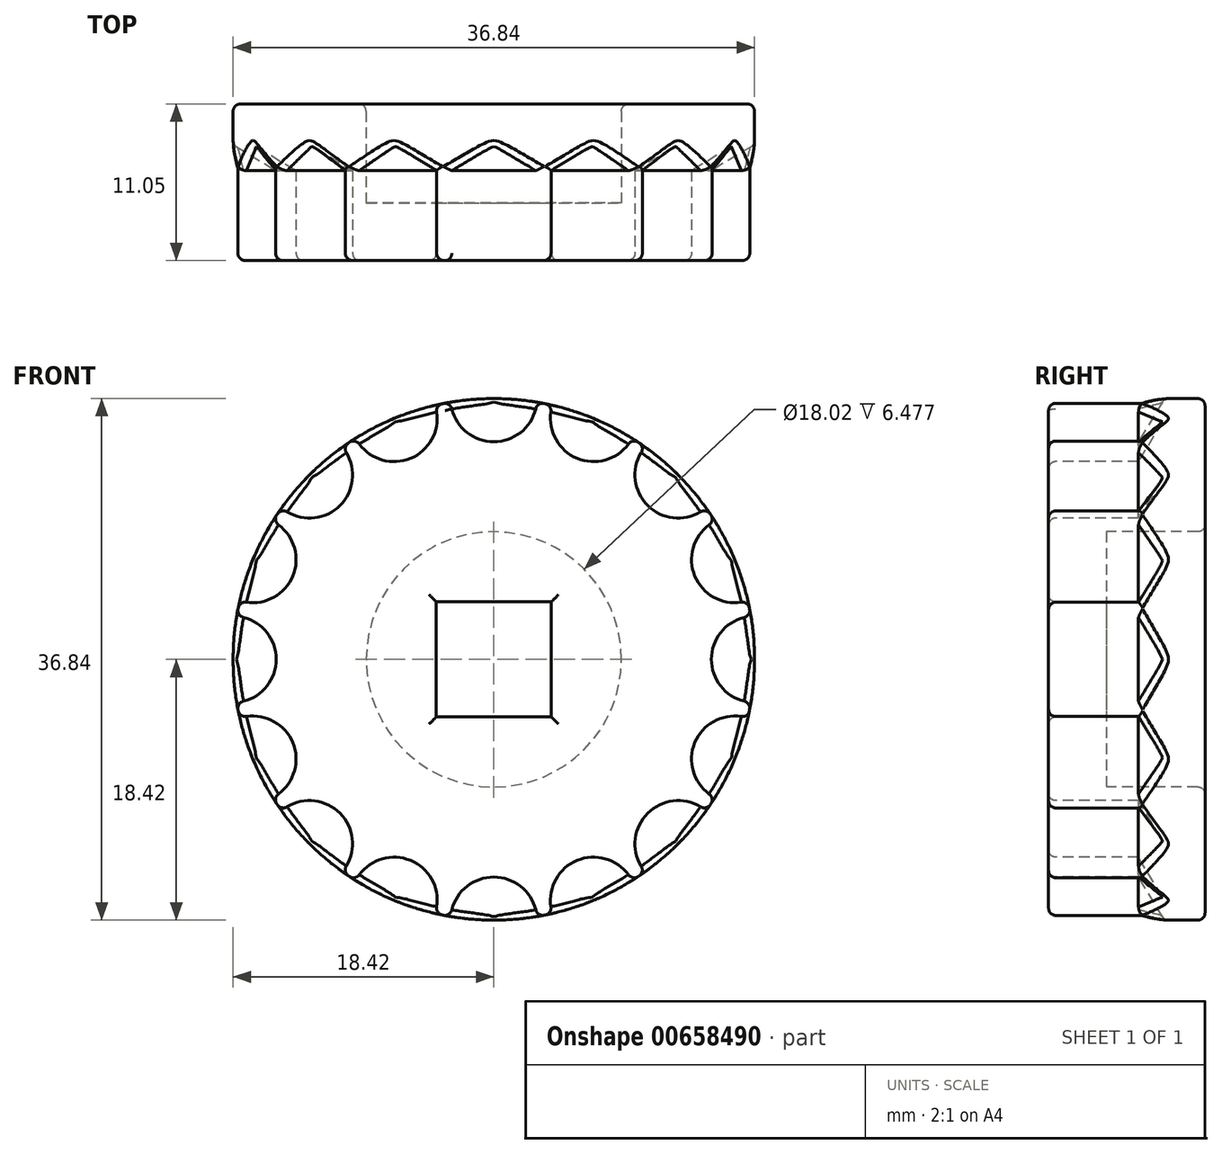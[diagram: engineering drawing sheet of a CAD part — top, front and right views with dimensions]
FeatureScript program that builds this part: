
annotation { "Feature Type Name" : "Feature", "Feature Type Description" : "" }
export const myFeature = defineFeature(function(context is Context, id is Id, definition is map)
    precondition{}
    {
        {
            var Q0;
            Q0=qCreatedBy(makeId("Front.planeOp"),FACE);
            var sketch = newSketch(context, id + "F0", { "sketchPlane" : qUnion([Q0])});
            skCircle(sketch, "E0", {"center": v(0, 0) * mm, "radius": 18.41 * mm});
            skLineSegment(sketch, "E1.bottom", {"start": v(-4.06, 4.06) * mm, "end": v(4.06, 4.06) * mm});
            skLineSegment(sketch, "E1.top", {"start": v(-4.06, -4.06) * mm, "end": v(4.06, -4.06) * mm});
            skLineSegment(sketch, "E1.left", {"start": v(-4.06, 4.06) * mm, "end": v(-4.06, -4.06) * mm});
            skLineSegment(sketch, "E1.right", {"start": v(4.06, 4.06) * mm, "end": v(4.06, -4.06) * mm});
            skSolve(sketch);
        }
        {
            var Q0;
            Q0=makeQuery(id+"F0.imprint","IMPRINT",FACE,{"disambiguationData":[TD([[makeQuery(id+"F0.imprint","IMPRINT",EDGE,{"derivedFrom":sQuery(id+"F0.wireOp",EDGE,"E0")}),1.0]])]});
            extrude(context, id + "F1", {"entities" : qUnion([Q0]), "depth" : 4.06 * mm, "offsetDistance" : 25.4 * mm});
        }
        {
            var Q0;
            Q0=makeQuery(id+"F1.opExtrude","CAP_FACE",FACE,{"disambiguationData":[OSD([sQuery(id+"F0.wireOp",EDGE,"E0"),sQuery(id+"F0.wireOp",EDGE,"9JpsgNl9-H64Q-FjUh-Arcb-bKjkUMni8Wci.bottom"),sQuery(id+"F0.wireOp",EDGE,"9JpsgNl9-H64Q-FjUh-Arcb-bKjkUMni8Wci.top"),sQuery(id+"F0.wireOp",EDGE,"9JpsgNl9-H64Q-FjUh-Arcb-bKjkUMni8Wci.left"),sQuery(id+"F0.wireOp",EDGE,"9JpsgNl9-H64Q-FjUh-Arcb-bKjkUMni8Wci.right")])],"isStart":true});
            var sketch = newSketch(context, id + "F2", { "sketchPlane" : qUnion([Q0])});
            skCircle(sketch, "E2", {"center": v(0, 0) * mm, "radius": 18.41 * mm});
            skCircle(sketch, "E3", {"center": v(0, 0) * mm, "radius": 9.01 * mm});
            skLineSegment(sketch, "E4", {"start": v(53.44, -8.32) * mm, "end": v(72.7, 0) * mm});
            skSolve(sketch);
        }
        {
            var Q0;
            Q0=makeQuery(id+"F2.imprint","IMPRINT",FACE,{"disambiguationData":[TD([[makeQuery(id+"F2.imprint","IMPRINT",EDGE,{"derivedFrom":sQuery(id+"F2.wireOp",EDGE,"E2")}),-1.0]])]});
            extrude(context, id + "F3", {"entities" : qUnion([Q0]), "operationType" : NewBodyOperationType.ADD, "depth" : 7 * mm, "offsetDistance" : 25.4 * mm});
        }
        {
            var Q0;
            Q0=makeQuery(id+"F1.opExtrude","CAP_FACE",FACE,{"disambiguationData":[OSD([sQuery(id+"F0.wireOp",EDGE,"E0"),sQuery(id+"F0.wireOp",EDGE,"9JpsgNl9-H64Q-FjUh-Arcb-bKjkUMni8Wci.bottom"),sQuery(id+"F0.wireOp",EDGE,"9JpsgNl9-H64Q-FjUh-Arcb-bKjkUMni8Wci.top"),sQuery(id+"F0.wireOp",EDGE,"9JpsgNl9-H64Q-FjUh-Arcb-bKjkUMni8Wci.left"),sQuery(id+"F0.wireOp",EDGE,"9JpsgNl9-H64Q-FjUh-Arcb-bKjkUMni8Wci.right")])],"isStart":false});
            var sketch = newSketch(context, id + "F4", { "sketchPlane" : qUnion([Q0])});
            skArc(sketch, "E5", {"start": v(0, 15.37) * mm, "mid": v(2.06, 16.17) * mm, "end": v(3.04, 18.16) * mm});
            skArc(sketch, "E6.MirrorCS", {"start": v(0, 15.37) * mm, "mid": v(-2.06, 16.17) * mm, "end": v(-3.04, 18.16) * mm});
            skArc(sketch, "E7.1.0", {"start": v(5.88, 14.2) * mm, "mid": v(4.28, 15.73) * mm, "end": v(4.14, 17.94) * mm});
            skArc(sketch, "E7.1.1", {"start": v(5.88, 14.2) * mm, "mid": v(8.1, 14.15) * mm, "end": v(9.76, 15.62) * mm});
            skArc(sketch, "E7.2.0", {"start": v(10.87, 10.87) * mm, "mid": v(9.98, 12.9) * mm, "end": v(10.7, 15) * mm});
            skArc(sketch, "E7.2.1", {"start": v(10.87, 10.87) * mm, "mid": v(12.9, 9.98) * mm, "end": v(15, 10.7) * mm});
            skPoint(sketch, "E7.center", {"position": v(0, 0) * mm});
            skLineSegment(sketch, "E7.anchor1", {"start": v(0, 0) * mm, "end": v(-3.04, 18.16) * mm, "construction": true});
            skLineSegment(sketch, "E7.anchor2", {"start": v(0, 0) * mm, "end": v(10.7, 15) * mm, "construction": true});
            skArc(sketch, "E8.1.0", {"start": v(14.2, -5.88) * mm, "mid": v(14.15, -8.1) * mm, "end": v(15.62, -9.76) * mm});
            skArc(sketch, "E8.1.1", {"start": v(14.2, -5.88) * mm, "mid": v(15.73, -4.28) * mm, "end": v(17.94, -4.14) * mm});
            skArc(sketch, "E8.1.2", {"start": v(15.37, 0) * mm, "mid": v(16.17, -2.06) * mm, "end": v(18.16, -3.04) * mm});
            skArc(sketch, "E8.1.3", {"start": v(15.37, 0) * mm, "mid": v(16.17, 2.06) * mm, "end": v(18.16, 3.04) * mm});
            skArc(sketch, "E8.1.4", {"start": v(14.2, 5.88) * mm, "mid": v(15.73, 4.28) * mm, "end": v(17.94, 4.14) * mm});
            skArc(sketch, "E8.1.5", {"start": v(14.2, 5.88) * mm, "mid": v(14.15, 8.1) * mm, "end": v(15.62, 9.76) * mm});
            skArc(sketch, "E8.2.0", {"start": v(0, -15.37) * mm, "mid": v(-2.06, -16.17) * mm, "end": v(-3.04, -18.16) * mm});
            skArc(sketch, "E8.2.1", {"start": v(0, -15.37) * mm, "mid": v(2.06, -16.17) * mm, "end": v(3.04, -18.16) * mm});
            skArc(sketch, "E8.2.2", {"start": v(5.88, -14.2) * mm, "mid": v(4.28, -15.73) * mm, "end": v(4.14, -17.94) * mm});
            skArc(sketch, "E8.2.3", {"start": v(5.88, -14.2) * mm, "mid": v(8.1, -14.15) * mm, "end": v(9.76, -15.62) * mm});
            skArc(sketch, "E8.2.4", {"start": v(10.87, -10.87) * mm, "mid": v(9.98, -12.9) * mm, "end": v(10.7, -15) * mm});
            skArc(sketch, "E8.2.5", {"start": v(10.87, -10.87) * mm, "mid": v(12.9, -9.98) * mm, "end": v(15, -10.7) * mm});
            skLineSegment(sketch, "E8.anchor1", {"start": v(0, 0) * mm, "end": v(10.87, 10.87) * mm, "construction": true});
            skLineSegment(sketch, "E8.anchor2", {"start": v(0, 0) * mm, "end": v(0, -15.37) * mm, "construction": true});
            skArc(sketch, "E9.1.0", {"start": v(-15.37, 0) * mm, "mid": v(-16.17, 2.06) * mm, "end": v(-18.16, 3.04) * mm});
            skArc(sketch, "E9.1.1", {"start": v(-15.37, 0) * mm, "mid": v(-16.17, -2.06) * mm, "end": v(-18.16, -3.04) * mm});
            skArc(sketch, "E9.1.2", {"start": v(-14.2, -5.88) * mm, "mid": v(-15.73, -4.28) * mm, "end": v(-17.94, -4.14) * mm});
            skArc(sketch, "E9.1.3", {"start": v(-14.2, -5.88) * mm, "mid": v(-14.15, -8.1) * mm, "end": v(-15.62, -9.76) * mm});
            skArc(sketch, "E9.1.4", {"start": v(-10.87, -10.87) * mm, "mid": v(-12.9, -9.98) * mm, "end": v(-15, -10.7) * mm});
            skArc(sketch, "E9.1.5", {"start": v(-10.87, -10.87) * mm, "mid": v(-9.98, -12.9) * mm, "end": v(-10.7, -15) * mm});
            skArc(sketch, "E9.1.6", {"start": v(-5.88, -14.2) * mm, "mid": v(-8.1, -14.15) * mm, "end": v(-9.76, -15.62) * mm});
            skArc(sketch, "E9.1.7", {"start": v(-5.88, -14.2) * mm, "mid": v(-4.28, -15.73) * mm, "end": v(-4.14, -17.94) * mm});
            skArc(sketch, "E9.2.2", {"start": v(-5.88, 14.2) * mm, "mid": v(-4.28, 15.73) * mm, "end": v(-4.14, 17.94) * mm});
            skArc(sketch, "E9.2.3", {"start": v(-5.88, 14.2) * mm, "mid": v(-8.1, 14.15) * mm, "end": v(-9.76, 15.62) * mm});
            skArc(sketch, "E9.2.4", {"start": v(-10.87, 10.87) * mm, "mid": v(-9.98, 12.9) * mm, "end": v(-10.7, 15) * mm});
            skArc(sketch, "E9.2.5", {"start": v(-10.87, 10.87) * mm, "mid": v(-12.9, 9.98) * mm, "end": v(-15, 10.7) * mm});
            skArc(sketch, "E9.2.6", {"start": v(-14.2, 5.88) * mm, "mid": v(-14.15, 8.1) * mm, "end": v(-15.62, 9.76) * mm});
            skArc(sketch, "E9.2.7", {"start": v(-14.2, 5.88) * mm, "mid": v(-15.73, 4.28) * mm, "end": v(-17.94, 4.14) * mm});
            skLineSegment(sketch, "E9.anchor1", {"start": v(0, 0) * mm, "end": v(-3.04, -18.16) * mm, "construction": true});
            skLineSegment(sketch, "E9.anchor2", {"start": v(0, 0) * mm, "end": v(3.04, 18.16) * mm, "construction": true});
            skSolve(sketch);
        }
        {
            var Q0;
            Q0=sQuery(id+"F4.wireOp",VERTEX,"E9.2.2.center");
            var Q1;
            Q1=sQuery(id+"F4.wireOp",VERTEX,"E9.2.5.center");
            var Q2;
            Q2=sQuery(id+"F4.wireOp",VERTEX,"E9.1.1.center");
            var Q3;
            Q3=sQuery(id+"F4.wireOp",VERTEX,"E9.1.3.center");
            var Q4;
            Q4=sQuery(id+"F4.wireOp",VERTEX,"E9.1.5.center");
            var Q5;
            Q5=sQuery(id+"F4.wireOp",VERTEX,"E9.1.7.center");
            var Q6;
            Q6=sQuery(id+"F4.wireOp",VERTEX,"E8.2.1.center");
            var Q7;
            Q7=sQuery(id+"F4.wireOp",VERTEX,"E8.2.3.center");
            var Q8;
            Q8=sQuery(id+"F4.wireOp",VERTEX,"E8.2.5.center");
            var Q9;
            Q9=sQuery(id+"F4.wireOp",VERTEX,"E8.1.1.center");
            var Q10;
            Q10=sQuery(id+"F4.wireOp",VERTEX,"E8.1.2.center");
            var Q11;
            Q11=sQuery(id+"F4.wireOp",VERTEX,"E8.1.5.center");
            var Q12;
            Q12=sQuery(id+"F4.wireOp",VERTEX,"E7.2.1.center");
            var Q13;
            Q13=sQuery(id+"F4.wireOp",VERTEX,"E7.1.1.center");
            var Q14;
            Q14=sQuery(id+"F4.wireOp",VERTEX,"E5.center");
            var Q15;
            Q15=sQuery(id+"F4.wireOp",VERTEX,"E9.2.6.center");
            var Q16;
            Q16=makeQuery(id+"F1.opExtrude","SWEPT_BODY",BODY,{"disambiguationData":[OSD([sQuery(id+"F0.wireOp",EDGE,"E0"),sQuery(id+"F0.wireOp",EDGE,"9JpsgNl9-H64Q-FjUh-Arcb-bKjkUMni8Wci.bottom"),sQuery(id+"F0.wireOp",EDGE,"9JpsgNl9-H64Q-FjUh-Arcb-bKjkUMni8Wci.top"),sQuery(id+"F0.wireOp",EDGE,"9JpsgNl9-H64Q-FjUh-Arcb-bKjkUMni8Wci.left"),sQuery(id+"F0.wireOp",EDGE,"9JpsgNl9-H64Q-FjUh-Arcb-bKjkUMni8Wci.right")])]});
            hole(context, id + "F5", {"style" : HoleStyle.SIMPLE, "endStyle" : HoleEndStyle.BLIND, "holeDiameter" : 6.1 * mm, "majorDiameter" : 6.35 * mm, "holeDepth" : 6.35 * mm, "isTappedThrough" : true, "tappedDepth" : 12.7 * mm, "tapClearance" : 3, "startFromSketch" : true, "locations" : qUnion([Q0, Q1, Q2, Q3, Q4, Q5, Q6, Q7, Q8, Q9, Q10, Q11, Q12, Q13, Q14, Q15]), "scope" : qUnion([Q16])});
        }
        {
            var Q0;
            Q0=makeQuery(id+"F1.opExtrude","CAP_FACE",FACE,{"disambiguationData":[OSD([sQuery(id+"F0.wireOp",EDGE,"E0"),sQuery(id+"F0.wireOp",EDGE,"9JpsgNl9-H64Q-FjUh-Arcb-bKjkUMni8Wci.bottom"),sQuery(id+"F0.wireOp",EDGE,"9JpsgNl9-H64Q-FjUh-Arcb-bKjkUMni8Wci.top"),sQuery(id+"F0.wireOp",EDGE,"9JpsgNl9-H64Q-FjUh-Arcb-bKjkUMni8Wci.left"),sQuery(id+"F0.wireOp",EDGE,"9JpsgNl9-H64Q-FjUh-Arcb-bKjkUMni8Wci.right")])],"isStart":false});
            var Q1;
            Q1=makeQuery(id+"F5.hole-1.boolean.opBoolean","INTERSECT",EDGE,{"disambiguationData":[OD(1.0)],"derivedFrom":[makeQuery(id+"F3.boolean.opBoolean","MERGE",FACE,{"derivedFrom":[makeQuery(id+"F1.opExtrude","SWEPT_FACE",FACE,{"disambiguationData":[OSD([sQuery(id+"F0.wireOp",EDGE,"E0")])]}),makeQuery(id+"F3.opExtrude","SWEPT_FACE",FACE,{"disambiguationData":[OSD([sQuery(id+"F2.wireOp",EDGE,"E2")])]})]}),makeQuery(id+"F5.hole-1.opRevolve","SWEPT_FACE",FACE,{"disambiguationData":[OSD([sQuery(id+"F5.hole-1.sketch.wireOp",EDGE,"core_line_2")])]})]});
            var Q2;
            Q2=makeQuery(id+"F5.hole-15.boolean.opBoolean","INTERSECT",EDGE,{"disambiguationData":[OD(0.0)],"derivedFrom":[makeQuery(id+"F3.boolean.opBoolean","MERGE",FACE,{"derivedFrom":[makeQuery(id+"F1.opExtrude","SWEPT_FACE",FACE,{"disambiguationData":[OSD([sQuery(id+"F0.wireOp",EDGE,"E0")])]}),makeQuery(id+"F3.opExtrude","SWEPT_FACE",FACE,{"disambiguationData":[OSD([sQuery(id+"F2.wireOp",EDGE,"E2")])]})]}),makeQuery(id+"F5.hole-15.opRevolve","SWEPT_FACE",FACE,{"disambiguationData":[OSD([sQuery(id+"F5.hole-15.sketch.wireOp",EDGE,"core_line_2")])]})]});
            var Q3;
            Q3=makeQuery(id+"F5.hole-15.boolean.opBoolean","INTERSECT",EDGE,{"disambiguationData":[OD(1.0)],"derivedFrom":[makeQuery(id+"F3.boolean.opBoolean","MERGE",FACE,{"derivedFrom":[makeQuery(id+"F1.opExtrude","SWEPT_FACE",FACE,{"disambiguationData":[OSD([sQuery(id+"F0.wireOp",EDGE,"E0")])]}),makeQuery(id+"F3.opExtrude","SWEPT_FACE",FACE,{"disambiguationData":[OSD([sQuery(id+"F2.wireOp",EDGE,"E2")])]})]}),makeQuery(id+"F5.hole-15.opRevolve","SWEPT_FACE",FACE,{"disambiguationData":[OSD([sQuery(id+"F5.hole-15.sketch.wireOp",EDGE,"core_line_2")])]})]});
            var Q4;
            Q4=makeQuery(id+"F5.hole-2.boolean.opBoolean","INTERSECT",EDGE,{"disambiguationData":[OD(1.0)],"derivedFrom":[makeQuery(id+"F3.boolean.opBoolean","MERGE",FACE,{"derivedFrom":[makeQuery(id+"F1.opExtrude","SWEPT_FACE",FACE,{"disambiguationData":[OSD([sQuery(id+"F0.wireOp",EDGE,"E0")])]}),makeQuery(id+"F3.opExtrude","SWEPT_FACE",FACE,{"disambiguationData":[OSD([sQuery(id+"F2.wireOp",EDGE,"E2")])]})]}),makeQuery(id+"F5.hole-2.opRevolve","SWEPT_FACE",FACE,{"disambiguationData":[OSD([sQuery(id+"F5.hole-2.sketch.wireOp",EDGE,"core_line_2")])]})]});
            var Q5;
            Q5=makeQuery(id+"F5.hole-2.boolean.opBoolean","INTERSECT",EDGE,{"disambiguationData":[OD(0.0)],"derivedFrom":[makeQuery(id+"F3.boolean.opBoolean","MERGE",FACE,{"derivedFrom":[makeQuery(id+"F1.opExtrude","SWEPT_FACE",FACE,{"disambiguationData":[OSD([sQuery(id+"F0.wireOp",EDGE,"E0")])]}),makeQuery(id+"F3.opExtrude","SWEPT_FACE",FACE,{"disambiguationData":[OSD([sQuery(id+"F2.wireOp",EDGE,"E2")])]})]}),makeQuery(id+"F5.hole-2.opRevolve","SWEPT_FACE",FACE,{"disambiguationData":[OSD([sQuery(id+"F5.hole-2.sketch.wireOp",EDGE,"core_line_2")])]})]});
            var Q6;
            Q6=makeQuery(id+"F5.hole-3.boolean.opBoolean","INTERSECT",EDGE,{"disambiguationData":[OD(1.0)],"derivedFrom":[makeQuery(id+"F3.boolean.opBoolean","MERGE",FACE,{"derivedFrom":[makeQuery(id+"F1.opExtrude","SWEPT_FACE",FACE,{"disambiguationData":[OSD([sQuery(id+"F0.wireOp",EDGE,"E0")])]}),makeQuery(id+"F3.opExtrude","SWEPT_FACE",FACE,{"disambiguationData":[OSD([sQuery(id+"F2.wireOp",EDGE,"E2")])]})]}),makeQuery(id+"F5.hole-3.opRevolve","SWEPT_FACE",FACE,{"disambiguationData":[OSD([sQuery(id+"F5.hole-3.sketch.wireOp",EDGE,"core_line_2")])]})]});
            var Q7;
            Q7=makeQuery(id+"F5.hole-4.boolean.opBoolean","INTERSECT",EDGE,{"disambiguationData":[OD(0.0)],"derivedFrom":[makeQuery(id+"F3.boolean.opBoolean","MERGE",FACE,{"derivedFrom":[makeQuery(id+"F1.opExtrude","SWEPT_FACE",FACE,{"disambiguationData":[OSD([sQuery(id+"F0.wireOp",EDGE,"E0")])]}),makeQuery(id+"F3.opExtrude","SWEPT_FACE",FACE,{"disambiguationData":[OSD([sQuery(id+"F2.wireOp",EDGE,"E2")])]})]}),makeQuery(id+"F5.hole-4.opRevolve","SWEPT_FACE",FACE,{"disambiguationData":[OSD([sQuery(id+"F5.hole-4.sketch.wireOp",EDGE,"core_line_2")])]})]});
            var Q8;
            Q8=makeQuery(id+"F5.hole-5.boolean.opBoolean","INTERSECT",EDGE,{"disambiguationData":[OD(1.0)],"derivedFrom":[makeQuery(id+"F3.boolean.opBoolean","MERGE",FACE,{"derivedFrom":[makeQuery(id+"F1.opExtrude","SWEPT_FACE",FACE,{"disambiguationData":[OSD([sQuery(id+"F0.wireOp",EDGE,"E0")])]}),makeQuery(id+"F3.opExtrude","SWEPT_FACE",FACE,{"disambiguationData":[OSD([sQuery(id+"F2.wireOp",EDGE,"E2")])]})]}),makeQuery(id+"F5.hole-5.opRevolve","SWEPT_FACE",FACE,{"disambiguationData":[OSD([sQuery(id+"F5.hole-5.sketch.wireOp",EDGE,"core_line_2")])]})]});
            var Q9;
            Q9=makeQuery(id+"F5.hole-5.boolean.opBoolean","INTERSECT",EDGE,{"disambiguationData":[OD(0.0)],"derivedFrom":[makeQuery(id+"F3.boolean.opBoolean","MERGE",FACE,{"derivedFrom":[makeQuery(id+"F1.opExtrude","SWEPT_FACE",FACE,{"disambiguationData":[OSD([sQuery(id+"F0.wireOp",EDGE,"E0")])]}),makeQuery(id+"F3.opExtrude","SWEPT_FACE",FACE,{"disambiguationData":[OSD([sQuery(id+"F2.wireOp",EDGE,"E2")])]})]}),makeQuery(id+"F5.hole-5.opRevolve","SWEPT_FACE",FACE,{"disambiguationData":[OSD([sQuery(id+"F5.hole-5.sketch.wireOp",EDGE,"core_line_2")])]})]});
            var Q10;
            Q10=makeQuery(id+"F5.hole-6.boolean.opBoolean","INTERSECT",EDGE,{"disambiguationData":[OD(1.0)],"derivedFrom":[makeQuery(id+"F3.boolean.opBoolean","MERGE",FACE,{"derivedFrom":[makeQuery(id+"F1.opExtrude","SWEPT_FACE",FACE,{"disambiguationData":[OSD([sQuery(id+"F0.wireOp",EDGE,"E0")])]}),makeQuery(id+"F3.opExtrude","SWEPT_FACE",FACE,{"disambiguationData":[OSD([sQuery(id+"F2.wireOp",EDGE,"E2")])]})]}),makeQuery(id+"F5.hole-6.opRevolve","SWEPT_FACE",FACE,{"disambiguationData":[OSD([sQuery(id+"F5.hole-6.sketch.wireOp",EDGE,"core_line_2")])]})]});
            var Q11;
            Q11=makeQuery(id+"F5.hole-4.boolean.opBoolean","INTERSECT",EDGE,{"disambiguationData":[OD(1.0)],"derivedFrom":[makeQuery(id+"F3.boolean.opBoolean","MERGE",FACE,{"derivedFrom":[makeQuery(id+"F1.opExtrude","SWEPT_FACE",FACE,{"disambiguationData":[OSD([sQuery(id+"F0.wireOp",EDGE,"E0")])]}),makeQuery(id+"F3.opExtrude","SWEPT_FACE",FACE,{"disambiguationData":[OSD([sQuery(id+"F2.wireOp",EDGE,"E2")])]})]}),makeQuery(id+"F5.hole-4.opRevolve","SWEPT_FACE",FACE,{"disambiguationData":[OSD([sQuery(id+"F5.hole-4.sketch.wireOp",EDGE,"core_line_2")])]})]});
            var Q12;
            Q12=makeQuery(id+"F5.hole-6.boolean.opBoolean","INTERSECT",EDGE,{"disambiguationData":[OD(0.0)],"derivedFrom":[makeQuery(id+"F3.boolean.opBoolean","MERGE",FACE,{"derivedFrom":[makeQuery(id+"F1.opExtrude","SWEPT_FACE",FACE,{"disambiguationData":[OSD([sQuery(id+"F0.wireOp",EDGE,"E0")])]}),makeQuery(id+"F3.opExtrude","SWEPT_FACE",FACE,{"disambiguationData":[OSD([sQuery(id+"F2.wireOp",EDGE,"E2")])]})]}),makeQuery(id+"F5.hole-6.opRevolve","SWEPT_FACE",FACE,{"disambiguationData":[OSD([sQuery(id+"F5.hole-6.sketch.wireOp",EDGE,"core_line_2")])]})]});
            var Q13;
            Q13=makeQuery(id+"F5.hole-7.boolean.opBoolean","INTERSECT",EDGE,{"disambiguationData":[OD(1.0)],"derivedFrom":[makeQuery(id+"F3.boolean.opBoolean","MERGE",FACE,{"derivedFrom":[makeQuery(id+"F1.opExtrude","SWEPT_FACE",FACE,{"disambiguationData":[OSD([sQuery(id+"F0.wireOp",EDGE,"E0")])]}),makeQuery(id+"F3.opExtrude","SWEPT_FACE",FACE,{"disambiguationData":[OSD([sQuery(id+"F2.wireOp",EDGE,"E2")])]})]}),makeQuery(id+"F5.hole-7.opRevolve","SWEPT_FACE",FACE,{"disambiguationData":[OSD([sQuery(id+"F5.hole-7.sketch.wireOp",EDGE,"core_line_2")])]})]});
            var Q14;
            Q14=makeQuery(id+"F5.hole-7.boolean.opBoolean","INTERSECT",EDGE,{"disambiguationData":[OD(0.0)],"derivedFrom":[makeQuery(id+"F3.boolean.opBoolean","MERGE",FACE,{"derivedFrom":[makeQuery(id+"F1.opExtrude","SWEPT_FACE",FACE,{"disambiguationData":[OSD([sQuery(id+"F0.wireOp",EDGE,"E0")])]}),makeQuery(id+"F3.opExtrude","SWEPT_FACE",FACE,{"disambiguationData":[OSD([sQuery(id+"F2.wireOp",EDGE,"E2")])]})]}),makeQuery(id+"F5.hole-7.opRevolve","SWEPT_FACE",FACE,{"disambiguationData":[OSD([sQuery(id+"F5.hole-7.sketch.wireOp",EDGE,"core_line_2")])]})]});
            var Q15;
            Q15=makeQuery(id+"F5.hole-8.boolean.opBoolean","INTERSECT",EDGE,{"disambiguationData":[OD(1.0)],"derivedFrom":[makeQuery(id+"F3.boolean.opBoolean","MERGE",FACE,{"derivedFrom":[makeQuery(id+"F1.opExtrude","SWEPT_FACE",FACE,{"disambiguationData":[OSD([sQuery(id+"F0.wireOp",EDGE,"E0")])]}),makeQuery(id+"F3.opExtrude","SWEPT_FACE",FACE,{"disambiguationData":[OSD([sQuery(id+"F2.wireOp",EDGE,"E2")])]})]}),makeQuery(id+"F5.hole-8.opRevolve","SWEPT_FACE",FACE,{"disambiguationData":[OSD([sQuery(id+"F5.hole-8.sketch.wireOp",EDGE,"core_line_2")])]})]});
            var Q16;
            Q16=makeQuery(id+"F5.hole-12.boolean.opBoolean","INTERSECT",EDGE,{"disambiguationData":[OD(0.0)],"derivedFrom":[makeQuery(id+"F3.boolean.opBoolean","MERGE",FACE,{"derivedFrom":[makeQuery(id+"F1.opExtrude","SWEPT_FACE",FACE,{"disambiguationData":[OSD([sQuery(id+"F0.wireOp",EDGE,"E0")])]}),makeQuery(id+"F3.opExtrude","SWEPT_FACE",FACE,{"disambiguationData":[OSD([sQuery(id+"F2.wireOp",EDGE,"E2")])]})]}),makeQuery(id+"F5.hole-12.opRevolve","SWEPT_FACE",FACE,{"disambiguationData":[OSD([sQuery(id+"F5.hole-12.sketch.wireOp",EDGE,"core_line_2")])]})]});
            var Q17;
            Q17=makeQuery(id+"F5.hole-13.boolean.opBoolean","INTERSECT",EDGE,{"disambiguationData":[OD(1.0)],"derivedFrom":[makeQuery(id+"F3.boolean.opBoolean","MERGE",FACE,{"derivedFrom":[makeQuery(id+"F1.opExtrude","SWEPT_FACE",FACE,{"disambiguationData":[OSD([sQuery(id+"F0.wireOp",EDGE,"E0")])]}),makeQuery(id+"F3.opExtrude","SWEPT_FACE",FACE,{"disambiguationData":[OSD([sQuery(id+"F2.wireOp",EDGE,"E2")])]})]}),makeQuery(id+"F5.hole-13.opRevolve","SWEPT_FACE",FACE,{"disambiguationData":[OSD([sQuery(id+"F5.hole-13.sketch.wireOp",EDGE,"core_line_2")])]})]});
            var Q18;
            Q18=makeQuery(id+"F5.hole-13.boolean.opBoolean","INTERSECT",EDGE,{"disambiguationData":[OD(0.0)],"derivedFrom":[makeQuery(id+"F3.boolean.opBoolean","MERGE",FACE,{"derivedFrom":[makeQuery(id+"F1.opExtrude","SWEPT_FACE",FACE,{"disambiguationData":[OSD([sQuery(id+"F0.wireOp",EDGE,"E0")])]}),makeQuery(id+"F3.opExtrude","SWEPT_FACE",FACE,{"disambiguationData":[OSD([sQuery(id+"F2.wireOp",EDGE,"E2")])]})]}),makeQuery(id+"F5.hole-13.opRevolve","SWEPT_FACE",FACE,{"disambiguationData":[OSD([sQuery(id+"F5.hole-13.sketch.wireOp",EDGE,"core_line_2")])]})]});
            var Q19;
            Q19=makeQuery(id+"F5.hole-14.boolean.opBoolean","INTERSECT",EDGE,{"disambiguationData":[OD(1.0)],"derivedFrom":[makeQuery(id+"F3.boolean.opBoolean","MERGE",FACE,{"derivedFrom":[makeQuery(id+"F1.opExtrude","SWEPT_FACE",FACE,{"disambiguationData":[OSD([sQuery(id+"F0.wireOp",EDGE,"E0")])]}),makeQuery(id+"F3.opExtrude","SWEPT_FACE",FACE,{"disambiguationData":[OSD([sQuery(id+"F2.wireOp",EDGE,"E2")])]})]}),makeQuery(id+"F5.hole-14.opRevolve","SWEPT_FACE",FACE,{"disambiguationData":[OSD([sQuery(id+"F5.hole-14.sketch.wireOp",EDGE,"core_line_2")])]})]});
            var Q20;
            Q20=makeQuery(id+"F5.hole-14.boolean.opBoolean","INTERSECT",EDGE,{"disambiguationData":[OD(0.0)],"derivedFrom":[makeQuery(id+"F3.boolean.opBoolean","MERGE",FACE,{"derivedFrom":[makeQuery(id+"F1.opExtrude","SWEPT_FACE",FACE,{"disambiguationData":[OSD([sQuery(id+"F0.wireOp",EDGE,"E0")])]}),makeQuery(id+"F3.opExtrude","SWEPT_FACE",FACE,{"disambiguationData":[OSD([sQuery(id+"F2.wireOp",EDGE,"E2")])]})]}),makeQuery(id+"F5.hole-14.opRevolve","SWEPT_FACE",FACE,{"disambiguationData":[OSD([sQuery(id+"F5.hole-14.sketch.wireOp",EDGE,"core_line_2")])]})]});
            var Q21;
            Q21=makeQuery(id+"F5.hole-0.boolean.opBoolean","INTERSECT",EDGE,{"disambiguationData":[OD(1.0)],"derivedFrom":[makeQuery(id+"F3.boolean.opBoolean","MERGE",FACE,{"derivedFrom":[makeQuery(id+"F1.opExtrude","SWEPT_FACE",FACE,{"disambiguationData":[OSD([sQuery(id+"F0.wireOp",EDGE,"E0")])]}),makeQuery(id+"F3.opExtrude","SWEPT_FACE",FACE,{"disambiguationData":[OSD([sQuery(id+"F2.wireOp",EDGE,"E2")])]})]}),makeQuery(id+"F5.hole-0.opRevolve","SWEPT_FACE",FACE,{"disambiguationData":[OSD([sQuery(id+"F5.hole-0.sketch.wireOp",EDGE,"core_line_2")])]})]});
            var Q22;
            Q22=makeQuery(id+"F5.hole-0.boolean.opBoolean","INTERSECT",EDGE,{"disambiguationData":[OD(0.0)],"derivedFrom":[makeQuery(id+"F3.boolean.opBoolean","MERGE",FACE,{"derivedFrom":[makeQuery(id+"F1.opExtrude","SWEPT_FACE",FACE,{"disambiguationData":[OSD([sQuery(id+"F0.wireOp",EDGE,"E0")])]}),makeQuery(id+"F3.opExtrude","SWEPT_FACE",FACE,{"disambiguationData":[OSD([sQuery(id+"F2.wireOp",EDGE,"E2")])]})]}),makeQuery(id+"F5.hole-0.opRevolve","SWEPT_FACE",FACE,{"disambiguationData":[OSD([sQuery(id+"F5.hole-0.sketch.wireOp",EDGE,"core_line_2")])]})]});
            var Q23;
            Q23=makeQuery(id+"F5.hole-1.boolean.opBoolean","INTERSECT",EDGE,{"disambiguationData":[OD(0.0)],"derivedFrom":[makeQuery(id+"F3.boolean.opBoolean","MERGE",FACE,{"derivedFrom":[makeQuery(id+"F1.opExtrude","SWEPT_FACE",FACE,{"disambiguationData":[OSD([sQuery(id+"F0.wireOp",EDGE,"E0")])]}),makeQuery(id+"F3.opExtrude","SWEPT_FACE",FACE,{"disambiguationData":[OSD([sQuery(id+"F2.wireOp",EDGE,"E2")])]})]}),makeQuery(id+"F5.hole-1.opRevolve","SWEPT_FACE",FACE,{"disambiguationData":[OSD([sQuery(id+"F5.hole-1.sketch.wireOp",EDGE,"core_line_2")])]})]});
            var Q24;
            Q24=makeQuery(id+"F5.hole-3.boolean.opBoolean","INTERSECT",EDGE,{"disambiguationData":[OD(0.0)],"derivedFrom":[makeQuery(id+"F3.boolean.opBoolean","MERGE",FACE,{"derivedFrom":[makeQuery(id+"F1.opExtrude","SWEPT_FACE",FACE,{"disambiguationData":[OSD([sQuery(id+"F0.wireOp",EDGE,"E0")])]}),makeQuery(id+"F3.opExtrude","SWEPT_FACE",FACE,{"disambiguationData":[OSD([sQuery(id+"F2.wireOp",EDGE,"E2")])]})]}),makeQuery(id+"F5.hole-3.opRevolve","SWEPT_FACE",FACE,{"disambiguationData":[OSD([sQuery(id+"F5.hole-3.sketch.wireOp",EDGE,"core_line_2")])]})]});
            var Q25;
            Q25=makeQuery(id+"F3.opExtrude","CAP_FACE",FACE,{"disambiguationData":[OSD([sQuery(id+"F2.wireOp",EDGE,"E2"),sQuery(id+"F2.wireOp",EDGE,"e4b4ab94-6fab-4abd-99d8-f8be7362d1ef.0"),sQuery(id+"F2.wireOp",EDGE,"e4b4ab94-6fab-4abd-99d8-f8be7362d1ef.1"),sQuery(id+"F2.wireOp",EDGE,"e4b4ab94-6fab-4abd-99d8-f8be7362d1ef.2"),sQuery(id+"F2.wireOp",EDGE,"e4b4ab94-6fab-4abd-99d8-f8be7362d1ef.3"),sQuery(id+"F2.wireOp",EDGE,"e4b4ab94-6fab-4abd-99d8-f8be7362d1ef.4"),sQuery(id+"F2.wireOp",EDGE,"e4b4ab94-6fab-4abd-99d8-f8be7362d1ef.5")])],"isStart":false});
            var Q26;
            {var subQ0=sQuery(id+"F0.wireOp",EDGE,"E0");var subQ2=sQuery(id+"F2.wireOp",EDGE,"E2");var subQ4=makeQuery(id+"F5.hole-8.opRevolve","SWEPT_FACE",FACE,{"disambiguationData":[OSD([sQuery(id+"F5.hole-8.sketch.wireOp",EDGE,"core_line_2")])]});var subQ5=makeQuery(id+"F5.hole-0.boolean.opBoolean","COPY",FACE,{"derivedFrom":makeQuery(id+"F5.hole-0.opRevolve","SWEPT_FACE",FACE,{"disambiguationData":[OSD([sQuery(id+"F5.hole-0.sketch.wireOp",EDGE,"core_line_2")])]})});Q26=makeQuery(id+"F5.hole-9.boolean.opBoolean","SPLIT",FACE,{"disambiguationData":[TD([makeQuery(id+"F5.hole-8.boolean.opBoolean","COPY",FACE,{"derivedFrom":subQ4})])],"derivedFrom":makeQuery(id+"F5.hole-8.boolean.opBoolean","SPLIT",FACE,{"disambiguationData":[TD([subQ5])],"derivedFrom":makeQuery(id+"F5.hole-7.boolean.opBoolean","SPLIT",FACE,{"disambiguationData":[TD([subQ5])],"derivedFrom":makeQuery(id+"F5.hole-6.boolean.opBoolean","SPLIT",FACE,{"disambiguationData":[TD([subQ5])],"derivedFrom":makeQuery(id+"F5.hole-5.boolean.opBoolean","SPLIT",FACE,{"disambiguationData":[TD([subQ5])],"derivedFrom":makeQuery(id+"F5.hole-4.boolean.opBoolean","SPLIT",FACE,{"disambiguationData":[TD([subQ5])],"derivedFrom":makeQuery(id+"F5.hole-3.boolean.opBoolean","SPLIT",FACE,{"disambiguationData":[TD([subQ5])],"derivedFrom":makeQuery(id+"F5.hole-2.boolean.opBoolean","SPLIT",FACE,{"disambiguationData":[TD([subQ5])],"derivedFrom":makeQuery(id+"F5.hole-1.boolean.opBoolean","SPLIT",FACE,{"disambiguationData":[OD(1.0)],"derivedFrom":makeQuery(id+"F3.boolean.opBoolean","MERGE",FACE,{"derivedFrom":[makeQuery(id+"F1.opExtrude","SWEPT_FACE",FACE,{"disambiguationData":[OSD([subQ0])]}),makeQuery(id+"F3.opExtrude","SWEPT_FACE",FACE,{"disambiguationData":[OSD([subQ2])]})]})})})})})})})})})});}
            var Q27;
            {var subQ0=sQuery(id+"F0.wireOp",EDGE,"E0");var subQ2=sQuery(id+"F2.wireOp",EDGE,"E2");var subQ4=makeQuery(id+"F5.hole-9.opRevolve","SWEPT_FACE",FACE,{"disambiguationData":[OSD([sQuery(id+"F5.hole-9.sketch.wireOp",EDGE,"core_line_2")])]});var subQ5=makeQuery(id+"F5.hole-0.boolean.opBoolean","COPY",FACE,{"derivedFrom":makeQuery(id+"F5.hole-0.opRevolve","SWEPT_FACE",FACE,{"disambiguationData":[OSD([sQuery(id+"F5.hole-0.sketch.wireOp",EDGE,"core_line_2")])]})});Q27=makeQuery(id+"F5.hole-10.boolean.opBoolean","SPLIT",FACE,{"disambiguationData":[TD([makeQuery(id+"F5.hole-9.boolean.opBoolean","COPY",FACE,{"derivedFrom":subQ4})])],"derivedFrom":makeQuery(id+"F5.hole-9.boolean.opBoolean","SPLIT",FACE,{"disambiguationData":[TD([subQ5])],"derivedFrom":makeQuery(id+"F5.hole-8.boolean.opBoolean","SPLIT",FACE,{"disambiguationData":[TD([subQ5])],"derivedFrom":makeQuery(id+"F5.hole-7.boolean.opBoolean","SPLIT",FACE,{"disambiguationData":[TD([subQ5])],"derivedFrom":makeQuery(id+"F5.hole-6.boolean.opBoolean","SPLIT",FACE,{"disambiguationData":[TD([subQ5])],"derivedFrom":makeQuery(id+"F5.hole-5.boolean.opBoolean","SPLIT",FACE,{"disambiguationData":[TD([subQ5])],"derivedFrom":makeQuery(id+"F5.hole-4.boolean.opBoolean","SPLIT",FACE,{"disambiguationData":[TD([subQ5])],"derivedFrom":makeQuery(id+"F5.hole-3.boolean.opBoolean","SPLIT",FACE,{"disambiguationData":[TD([subQ5])],"derivedFrom":makeQuery(id+"F5.hole-2.boolean.opBoolean","SPLIT",FACE,{"disambiguationData":[TD([subQ5])],"derivedFrom":makeQuery(id+"F5.hole-1.boolean.opBoolean","SPLIT",FACE,{"disambiguationData":[OD(1.0)],"derivedFrom":makeQuery(id+"F3.boolean.opBoolean","MERGE",FACE,{"derivedFrom":[makeQuery(id+"F1.opExtrude","SWEPT_FACE",FACE,{"disambiguationData":[OSD([subQ0])]}),makeQuery(id+"F3.opExtrude","SWEPT_FACE",FACE,{"disambiguationData":[OSD([subQ2])]})]})})})})})})})})})})});}
            var Q28;
            {var subQ0=sQuery(id+"F0.wireOp",EDGE,"E0");var subQ2=sQuery(id+"F2.wireOp",EDGE,"E2");var subQ4=makeQuery(id+"F5.hole-10.opRevolve","SWEPT_FACE",FACE,{"disambiguationData":[OSD([sQuery(id+"F5.hole-10.sketch.wireOp",EDGE,"core_line_2")])]});var subQ5=makeQuery(id+"F5.hole-0.boolean.opBoolean","COPY",FACE,{"derivedFrom":makeQuery(id+"F5.hole-0.opRevolve","SWEPT_FACE",FACE,{"disambiguationData":[OSD([sQuery(id+"F5.hole-0.sketch.wireOp",EDGE,"core_line_2")])]})});Q28=makeQuery(id+"F5.hole-11.boolean.opBoolean","SPLIT",FACE,{"disambiguationData":[TD([makeQuery(id+"F5.hole-10.boolean.opBoolean","COPY",FACE,{"derivedFrom":subQ4})])],"derivedFrom":makeQuery(id+"F5.hole-10.boolean.opBoolean","SPLIT",FACE,{"disambiguationData":[TD([subQ5])],"derivedFrom":makeQuery(id+"F5.hole-9.boolean.opBoolean","SPLIT",FACE,{"disambiguationData":[TD([subQ5])],"derivedFrom":makeQuery(id+"F5.hole-8.boolean.opBoolean","SPLIT",FACE,{"disambiguationData":[TD([subQ5])],"derivedFrom":makeQuery(id+"F5.hole-7.boolean.opBoolean","SPLIT",FACE,{"disambiguationData":[TD([subQ5])],"derivedFrom":makeQuery(id+"F5.hole-6.boolean.opBoolean","SPLIT",FACE,{"disambiguationData":[TD([subQ5])],"derivedFrom":makeQuery(id+"F5.hole-5.boolean.opBoolean","SPLIT",FACE,{"disambiguationData":[TD([subQ5])],"derivedFrom":makeQuery(id+"F5.hole-4.boolean.opBoolean","SPLIT",FACE,{"disambiguationData":[TD([subQ5])],"derivedFrom":makeQuery(id+"F5.hole-3.boolean.opBoolean","SPLIT",FACE,{"disambiguationData":[TD([subQ5])],"derivedFrom":makeQuery(id+"F5.hole-2.boolean.opBoolean","SPLIT",FACE,{"disambiguationData":[TD([subQ5])],"derivedFrom":makeQuery(id+"F5.hole-1.boolean.opBoolean","SPLIT",FACE,{"disambiguationData":[OD(1.0)],"derivedFrom":makeQuery(id+"F3.boolean.opBoolean","MERGE",FACE,{"derivedFrom":[makeQuery(id+"F1.opExtrude","SWEPT_FACE",FACE,{"disambiguationData":[OSD([subQ0])]}),makeQuery(id+"F3.opExtrude","SWEPT_FACE",FACE,{"disambiguationData":[OSD([subQ2])]})]})})})})})})})})})})})});}
            var Q29;
            {var subQ0=sQuery(id+"F0.wireOp",EDGE,"E0");var subQ2=sQuery(id+"F2.wireOp",EDGE,"E2");var subQ4=makeQuery(id+"F5.hole-11.opRevolve","SWEPT_FACE",FACE,{"disambiguationData":[OSD([sQuery(id+"F5.hole-11.sketch.wireOp",EDGE,"core_line_2")])]});var subQ5=makeQuery(id+"F5.hole-0.boolean.opBoolean","COPY",FACE,{"derivedFrom":makeQuery(id+"F5.hole-0.opRevolve","SWEPT_FACE",FACE,{"disambiguationData":[OSD([sQuery(id+"F5.hole-0.sketch.wireOp",EDGE,"core_line_2")])]})});Q29=makeQuery(id+"F5.hole-12.boolean.opBoolean","SPLIT",FACE,{"disambiguationData":[TD([makeQuery(id+"F5.hole-11.boolean.opBoolean","COPY",FACE,{"derivedFrom":subQ4})])],"derivedFrom":makeQuery(id+"F5.hole-11.boolean.opBoolean","SPLIT",FACE,{"disambiguationData":[TD([subQ5])],"derivedFrom":makeQuery(id+"F5.hole-10.boolean.opBoolean","SPLIT",FACE,{"disambiguationData":[TD([subQ5])],"derivedFrom":makeQuery(id+"F5.hole-9.boolean.opBoolean","SPLIT",FACE,{"disambiguationData":[TD([subQ5])],"derivedFrom":makeQuery(id+"F5.hole-8.boolean.opBoolean","SPLIT",FACE,{"disambiguationData":[TD([subQ5])],"derivedFrom":makeQuery(id+"F5.hole-7.boolean.opBoolean","SPLIT",FACE,{"disambiguationData":[TD([subQ5])],"derivedFrom":makeQuery(id+"F5.hole-6.boolean.opBoolean","SPLIT",FACE,{"disambiguationData":[TD([subQ5])],"derivedFrom":makeQuery(id+"F5.hole-5.boolean.opBoolean","SPLIT",FACE,{"disambiguationData":[TD([subQ5])],"derivedFrom":makeQuery(id+"F5.hole-4.boolean.opBoolean","SPLIT",FACE,{"disambiguationData":[TD([subQ5])],"derivedFrom":makeQuery(id+"F5.hole-3.boolean.opBoolean","SPLIT",FACE,{"disambiguationData":[TD([subQ5])],"derivedFrom":makeQuery(id+"F5.hole-2.boolean.opBoolean","SPLIT",FACE,{"disambiguationData":[TD([subQ5])],"derivedFrom":makeQuery(id+"F5.hole-1.boolean.opBoolean","SPLIT",FACE,{"disambiguationData":[OD(1.0)],"derivedFrom":makeQuery(id+"F3.boolean.opBoolean","MERGE",FACE,{"derivedFrom":[makeQuery(id+"F1.opExtrude","SWEPT_FACE",FACE,{"disambiguationData":[OSD([subQ0])]}),makeQuery(id+"F3.opExtrude","SWEPT_FACE",FACE,{"disambiguationData":[OSD([subQ2])]})]})})})})})})})})})})})})});}
            fillet(context, id + "F6", {"entities" : qUnion([Q0, Q1, Q2, Q3, Q4, Q5, Q6, Q7, Q8, Q9, Q10, Q11, Q12, Q13, Q14, Q15, Q16, Q17, Q18, Q19, Q20, Q21, Q22, Q23, Q24, Q25, Q26, Q27, Q28, Q29]), "radius" : 0.5 * mm, "tangentPropagation" : true, "allowEdgeOverflow" : false});
        }
    });
